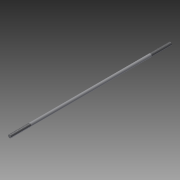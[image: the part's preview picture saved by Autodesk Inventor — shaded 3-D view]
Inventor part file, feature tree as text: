
AUTODESK INVENTOR PART (.ipt)
format: ipt  version: 2015 (Build 190159000, 159)  size: 70,144 bytes
history: native  units: mm
features: thread x2, extrude x1, sketch x1
ambient origin geometry x8: Origin, YZ Plane, XZ Plane, XY Plane, X Axis, Y Axis, Z Axis, Center Point
bodies: Solid1 (feature_tree)
feature tree (4):
  extrude  "Extrusion1"  Depth=160.0mm TaperAngle=0.0deg
  thread  "Thread1"  [1 undecoded]
  thread  "Thread2"  [1 undecoded]
  sketch  "Sketch1"  dims[d0=3.0mm d1=160.0mm d2=0.0mm d3=20.0mm d4=0.0mm d5=20.0mm d6=0.0mm]
note: 2 required parameter values undecoded (feature->parameter linkage not recoverable at this tier; creation-order binding heuristic only, values carry confidence <= 0.55)
